# Revit family: Furniture_Storage_Spacestor_Forte Credenza
name_source: partatom
category: Generic Models
revit_build: Autodesk Revit 2015 (Build: 20140223_1515(x64)
units: mm (PartAtom-declared; Revit-internal decimal feet)

## types (4) — shared parameters
Spacestor_Forte Credenza_Casework = Spacestor White

## per-type parameters (varying)
| type | 3 door | Door Number | Foot Centres | Foot Number | Spacestor_Forte Credenza_Foot | Spacestor_Forte Credenza_Handle | Width |
| 2-door - 814w x 500d x 700h | No | 1 | 700 mm  [stored 2.29659 ft] | 2 | <By Category> | <By Category> | 814 mm  [stored 2.6706 ft] |
| 4-door - 1628w x 500d x 700h | No | 2 | 758 mm  [stored 2.48688 ft] | 3 | <By Category> | <By Category> | 1628 mm  [stored 5.34121 ft] |
| 6-door - 2442w x 500d x 700h | No | 3 | 758 mm  [stored 2.48688 ft] | 4 | Spacestor Gray Plastic | Spacestor Polished Steel | 2442 mm  [stored 8.01181 ft] |
| 3-door - 1220w x 500d x 700h | Yes | 1 | 1106 mm  [stored 3.62861 ft] | 2 | <By Category> | <By Category> | 1221 mm  [stored 4.00591 ft] |

note: [stored X ft] marks values corroborated as IEEE doubles in the binary element streams (Revit-internal decimal feet)

## geometry (parser evidence)
native form markers: Sweep x20
no freeform markers — native parametric forms only
